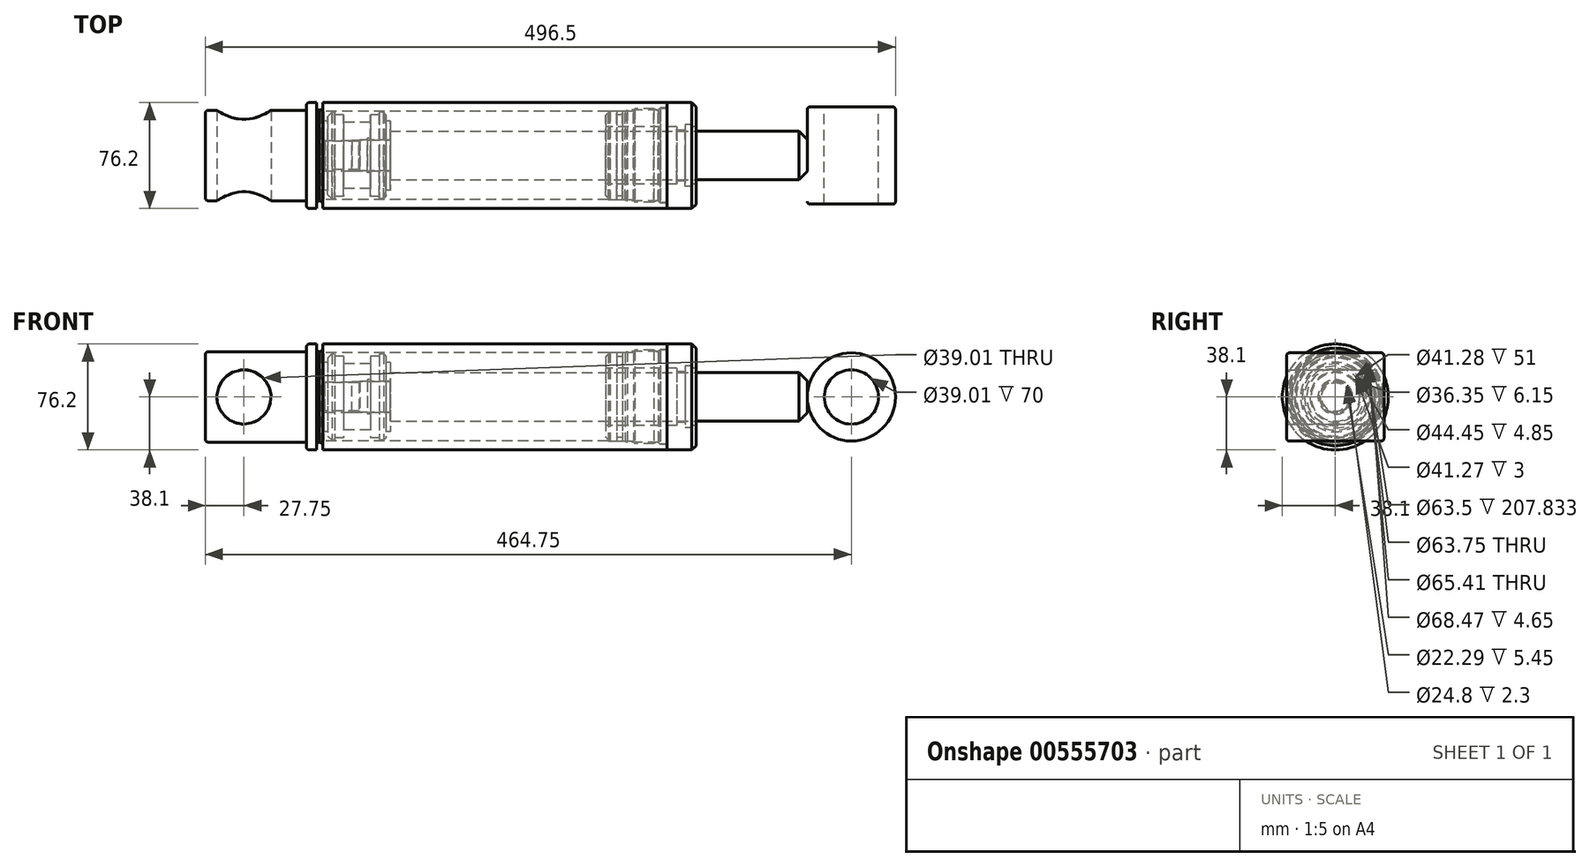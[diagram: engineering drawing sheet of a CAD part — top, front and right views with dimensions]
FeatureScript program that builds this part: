
annotation { "Feature Type Name" : "Feature", "Feature Type Description" : "" }
export const myFeature = defineFeature(function(context is Context, id is Id, definition is map)
    precondition{}
    {
        {
            var Q0;
            Q0=qCreatedBy(makeId("Front.planeOp"),FACE);
            var sketch = newSketch(context, id + "F0", { "sketchPlane" : qUnion([Q0])});
            skLineSegment(sketch, "E0", {"start": v(0, 0) * mm, "end": v(0, 31.22) * mm});
            skArc(sketch, "E1", {"start": v(0, 31.23) * mm, "mid": v(-0.15, 31.58) * mm, "end": v(-0.5, 31.73) * mm});
            skLineSegment(sketch, "E2", {"start": v(-0.5, 31.73) * mm, "end": v(-1.72, 31.73) * mm});
            skLineSegment(sketch, "E3", {"start": v(-1.72, 31.73) * mm, "end": v(-2.42, 31.37) * mm});
            skArc(sketch, "E4", {"start": v(-2.42, 31.37) * mm, "mid": v(-2.8, 31.38) * mm, "end": v(-3, 31.73) * mm});
            skLineSegment(sketch, "E5", {"start": v(-3, 31.73) * mm, "end": v(-3, 32.62) * mm});
            skArc(sketch, "E6", {"start": v(-5, 34.62) * mm, "mid": v(-4.41, 33.21) * mm, "end": v(-3, 32.62) * mm});
            skLineSegment(sketch, "E7", {"start": v(-5, 34.62) * mm, "end": v(-5, 38.1) * mm});
            skLineSegment(sketch, "E8", {"start": v(-5, 38.1) * mm, "end": v(-10.25, 38.1) * mm});
            skArc(sketch, "E9", {"start": v(-10.25, 38.1) * mm, "mid": v(-11.66, 37.51) * mm, "end": v(-12.25, 36.1) * mm});
            skLineSegment(sketch, "E10", {"start": v(-12.25, 36.1) * mm, "end": v(-12.25, 33.3) * mm});
            skLineSegment(sketch, "E11", {"start": v(-13.05, 32.5) * mm, "end": v(-83, 32.5) * mm});
            skArc(sketch, "E12", {"start": v(-83, 32.5) * mm, "mid": v(-84.41, 31.91) * mm, "end": v(-85, 30.5) * mm});
            skLineSegment(sketch, "E13", {"start": v(-85, 30.5) * mm, "end": v(-85, 0) * mm});
            skLineSegment(sketch, "E14", {"start": v(-85, 0) * mm, "end": v(0, 0) * mm});
            skPoint(sketch, "E15.visualSharp", {"position": v(-12.25, 32.5) * mm});
            skArc(sketch, "E15.filletArc", {"start": v(-13.05, 32.5) * mm, "mid": v(-12.48, 32.73) * mm, "end": v(-12.25, 33.3) * mm});
            skSolve(sketch);
        }
        {
            var Q0;
            Q0 = qSketchRegion(id + "F0", true);
            var Q1;
            Q1=sQuery(id+"F0.wireOp",EDGE,"E14");
            revolve(context, id + "F1", {"entities" : qUnion([Q0]), "axis" : qUnion([Q1]), "revolveType" : RevolveType.FULL});
        }
        {
            var Q0;
            Q0=qCreatedBy(makeId("Front.planeOp"),FACE);
            var sketch = newSketch(context, id + "F2", { "sketchPlane" : qUnion([Q0])});
            skCircle(sketch, "E16", {"center": v(-57.25, 0) * mm, "radius": 19.5 * mm});
            skSolve(sketch);
        }
        {
            var Q0;
            Q0=makeQuery(id+"F2.imprint","IMPRINT",FACE,{"disambiguationData":[TD([[makeQuery(id+"F2.imprint","IMPRINT",EDGE,{"derivedFrom":sQuery(id+"F2.wireOp",EDGE,"E16")}),1.0]])]});
            extrude(context, id + "F3", {"entities" : qUnion([Q0]), "operationType" : NewBodyOperationType.REMOVE, "endBound" : BoundingType.THROUGH_ALL, "oppositeDirection" : true, "depth" : 25 * mm, "offsetDistance" : 25 * mm, "hasSecondDirection" : true, "secondDirectionBound" : BoundingType.THROUGH_ALL, "secondDirectionOppositeDirection" : false, "secondDirectionDepth" : 25 * mm});
        }
        {
            var Q0;
            Q0=qCreatedBy(makeId("Front.planeOp"),FACE);
            var sketch = newSketch(context, id + "F4", { "sketchPlane" : qUnion([Q0])});
            skLineSegment(sketch, "E17", {"start": v(0, 25) * mm, "end": v(3, 25) * mm});
            skLineSegment(sketch, "E18", {"start": v(3, 25) * mm, "end": v(3, 28.05) * mm});
            skLineSegment(sketch, "E19", {"start": v(3, 28.05) * mm, "end": v(6, 31.05) * mm});
            skLineSegment(sketch, "E20", {"start": v(6, 31.05) * mm, "end": v(7.9, 31.05) * mm});
            skLineSegment(sketch, "E21", {"start": v(7.9, 31.05) * mm, "end": v(7.9, 29.45) * mm});
            skLineSegment(sketch, "E22", {"start": v(7.9, 29.45) * mm, "end": v(14.25, 29.45) * mm});
            skLineSegment(sketch, "E23", {"start": v(14.25, 29.45) * mm, "end": v(14.25, 23.8) * mm});
            skLineSegment(sketch, "E24", {"start": v(14.25, 23.8) * mm, "end": v(33.75, 23.81) * mm});
            skLineSegment(sketch, "E25", {"start": v(33.75, 23.81) * mm, "end": v(33.75, 12.4) * mm});
            skLineSegment(sketch, "E26", {"start": v(33.75, 12.4) * mm, "end": v(31.45, 12.4) * mm});
            skLineSegment(sketch, "E27", {"start": v(31.45, 12.4) * mm, "end": v(31.45, 11.15) * mm});
            skLineSegment(sketch, "E28", {"start": v(31.45, 11.14) * mm, "end": v(26, 11.14) * mm});
            skLineSegment(sketch, "E29", {"start": v(0, 25) * mm, "end": v(0, 11.14) * mm});
            skLineSegment(sketch, "E30", {"start": v(0, 11.14) * mm, "end": v(0.59, 10.12) * mm});
            skLineSegment(sketch, "E31", {"start": v(0.59, 10.12) * mm, "end": v(25.41, 10.12) * mm});
            skLineSegment(sketch, "E32", {"start": v(25.41, 10.12) * mm, "end": v(26, 11.15) * mm});
            skLineSegment(sketch, "E33", {"start": v(0, 0) * mm, "end": v(54.85, 0) * mm, "construction": true});
            skSolve(sketch);
        }
        {
            var Q0;
            Q0=makeQuery(id+"F4.imprint","IMPRINT",FACE,{"disambiguationData":[TD([[makeQuery(id+"F4.imprint","IMPRINT",EDGE,{"derivedFrom":sQuery(id+"F4.wireOp",EDGE,"E17")}),-1.0]])]});
            var Q1;
            Q1=sQuery(id+"F4.wireOp",EDGE,"E33");
            revolve(context, id + "F5", {"entities" : qUnion([Q0]), "axis" : qUnion([Q1]), "revolveType" : RevolveType.FULL});
        }
        {
            var Q0;
            Q0=qCreatedBy(makeId("Front.planeOp"),FACE);
            var sketch = newSketch(context, id + "F6", { "sketchPlane" : qUnion([Q0])});
            skLineSegment(sketch, "E34", {"start": v(33.75, 11.13) * mm, "end": v(33.75, 29.45) * mm});
            skLineSegment(sketch, "E35", {"start": v(33.75, 29.45) * mm, "end": v(40.1, 29.45) * mm});
            skLineSegment(sketch, "E36", {"start": v(40.1, 29.45) * mm, "end": v(40.1, 31.05) * mm});
            skLineSegment(sketch, "E37", {"start": v(40.1, 31.05) * mm, "end": v(43.4, 31.05) * mm});
            skLineSegment(sketch, "E38", {"start": v(43.4, 31.05) * mm, "end": v(45, 29.45) * mm});
            skLineSegment(sketch, "E39", {"start": v(45, 29.45) * mm, "end": v(45, 25) * mm});
            skLineSegment(sketch, "E40", {"start": v(45, 25) * mm, "end": v(48, 25) * mm});
            skLineSegment(sketch, "E41", {"start": v(48, 25) * mm, "end": v(48, 11.13) * mm});
            skLineSegment(sketch, "E42", {"start": v(48, 11.13) * mm, "end": v(33.75, 11.13) * mm});
            skPoint(sketch, "E43.orphan", {"position": v(33.75, 0) * mm});
            skLineSegment(sketch, "E44", {"start": v(33.75, 0) * mm, "end": v(71.94, 0) * mm, "construction": true});
            skSolve(sketch);
        }
        {
            var Q0;
            Q0=makeQuery(id+"F6.imprint","IMPRINT",FACE,{"disambiguationData":[TD([[makeQuery(id+"F6.imprint","IMPRINT",EDGE,{"derivedFrom":sQuery(id+"F6.wireOp",EDGE,"E34")}),-1.0]])]});
            var Q1;
            Q1=sQuery(id+"F6.wireOp",EDGE,"E44");
            var Q2;
            Q2=sQuery(id+"F6.wireOp",EDGE,"E44");
            revolve(context, id + "F7", {"entities" : qUnion([Q0]), "surfaceEntities" : qUnion([Q1]), "axis" : qUnion([Q2]), "revolveType" : RevolveType.FULL});
        }
        {
            var Q0;
            Q0=qCreatedBy(makeId("Front.planeOp"),FACE);
            var sketch = newSketch(context, id + "F8", { "sketchPlane" : qUnion([Q0])});
            skLineSegment(sketch, "E45", {"start": v(0.5, 0) * mm, "end": v(0.5, 10.13) * mm});
            skLineSegment(sketch, "E46", {"start": v(0.5, 10.13) * mm, "end": v(1, 11) * mm});
            skLineSegment(sketch, "E47", {"start": v(1, 11) * mm, "end": v(20.33, 11) * mm});
            skLineSegment(sketch, "E48", {"start": v(20.33, 11) * mm, "end": v(20.5, 11.1) * mm});
            skLineSegment(sketch, "E49", {"start": v(20.5, 11.1) * mm, "end": v(48, 11.1) * mm});
            skLineSegment(sketch, "E50", {"start": v(348, 11.46) * mm, "end": v(348, 0) * mm});
            skLineSegment(sketch, "E51", {"start": v(348, 0) * mm, "end": v(0.5, 0) * mm});
            skLineSegment(sketch, "E52", {"start": v(48, 11.1) * mm, "end": v(48, 17.46) * mm});
            skLineSegment(sketch, "E53", {"start": v(48, 17.46) * mm, "end": v(342, 17.46) * mm});
            skLineSegment(sketch, "E54", {"start": v(342, 17.46) * mm, "end": v(348, 11.46) * mm});
            skSolve(sketch);
        }
        {
            var Q0;
            Q0=makeQuery(id+"F8.imprint","IMPRINT",FACE,{"disambiguationData":[TD([[makeQuery(id+"F8.imprint","IMPRINT",EDGE,{"derivedFrom":sQuery(id+"F8.wireOp",EDGE,"E45")}),-1.0]])]});
            var Q1;
            Q1=sQuery(id+"F8.wireOp",EDGE,"E51");
            revolve(context, id + "F9", {"entities" : qUnion([Q0]), "axis" : qUnion([Q1]), "revolveType" : RevolveType.FULL});
        }
        {
            var Q0;
            Q0=qCreatedBy(makeId("Front.planeOp"),FACE);
            var sketch = newSketch(context, id + "F10", { "sketchPlane" : qUnion([Q0])});
            skCircle(sketch, "E55", {"center": v(379.75, 0) * mm, "radius": 31.75 * mm});
            skCircle(sketch, "E56", {"center": v(379.75, 0) * mm, "radius": 19.5 * mm});
            skSolve(sketch);
        }
        {
            var Q0;
            Q0=makeQuery(id+"F10.imprint","IMPRINT",FACE,{"disambiguationData":[TD([[makeQuery(id+"F10.imprint","IMPRINT",EDGE,{"derivedFrom":sQuery(id+"F10.wireOp",EDGE,"E55")}),1.0]])]});
            extrude(context, id + "F11", {"entities" : qUnion([Q0]), "depth" : 35 * mm, "offsetDistance" : 25 * mm, "hasSecondDirection" : true, "secondDirectionOppositeDirection" : true, "secondDirectionDepth" : 35 * mm});
        }
        {
            var Q0;
            Q0=makeQuery(id+"F11.opExtrude","CAP_EDGE",EDGE,{"disambiguationData":[OSD([sQuery(id+"F10.wireOp",EDGE,"E55")])],"isStart":true});
            var Q1;
            Q1=makeQuery(id+"F11.opExtrude","CAP_EDGE",EDGE,{"disambiguationData":[OSD([sQuery(id+"F10.wireOp",EDGE,"E55")])],"isStart":false});
            fillet(context, id + "F12", {"entities" : qUnion([Q0, Q1]), "radius" : 2 * mm, "tangentPropagation" : true, "allowEdgeOverflow" : false});
        }
        {
            var Q0;
            Q0=qCreatedBy(makeId("Front.planeOp"),FACE);
            var sketch = newSketch(context, id + "F13", { "sketchPlane" : qUnion([Q0])});
            skLineSegment(sketch, "E57", {"start": v(-3, 31.75) * mm, "end": v(204.83, 31.75) * mm});
            skLineSegment(sketch, "E58", {"start": v(204.83, 31.75) * mm, "end": v(205.05, 31.88) * mm});
            skLineSegment(sketch, "E59", {"start": v(205.05, 31.88) * mm, "end": v(217.01, 31.88) * mm});
            skLineSegment(sketch, "E60", {"start": v(217.01, 31.88) * mm, "end": v(218.45, 32.7) * mm});
            skLineSegment(sketch, "E61", {"start": v(218.45, 32.7) * mm, "end": v(240.82, 32.7) * mm});
            skLineSegment(sketch, "E62", {"start": v(240.82, 32.7) * mm, "end": v(242.35, 34.24) * mm});
            skLineSegment(sketch, "E63", {"start": v(242.35, 34.24) * mm, "end": v(247, 34.24) * mm});
            skLineSegment(sketch, "E64", {"start": v(247, 34.24) * mm, "end": v(247, 38.1) * mm});
            skLineSegment(sketch, "E65", {"start": v(247, 38.1) * mm, "end": v(-0.5, 38.1) * mm});
            skLineSegment(sketch, "E66", {"start": v(-0.5, 38.1) * mm, "end": v(-0.5, 35.12) * mm});
            skArc(sketch, "E67", {"start": v(-0.5, 35.12) * mm, "mid": v(-1.23, 33.36) * mm, "end": v(-3, 32.62) * mm});
            skLineSegment(sketch, "E68", {"start": v(-3, 32.62) * mm, "end": v(-3, 31.75) * mm});
            skLineSegment(sketch, "E69", {"start": v(0, 0) * mm, "end": v(80.8, 0) * mm, "construction": true});
            skSolve(sketch);
        }
        {
            var Q0;
            Q0 = qSketchRegion(id + "F13", true);
            var Q1;
            Q1=sQuery(id+"F13.wireOp",EDGE,"E69");
            revolve(context, id + "F14", {"entities" : qUnion([Q0]), "axis" : qUnion([Q1]), "revolveType" : RevolveType.FULL});
        }
        {
            var Q0;
            Q0=qCreatedBy(makeId("Front.planeOp"),FACE);
            var sketch = newSketch(context, id + "F15", { "sketchPlane" : qUnion([Q0])});
            skLineSegment(sketch, "E70", {"start": v(247, 38.1) * mm, "end": v(265, 38.1) * mm});
            skLineSegment(sketch, "E71", {"start": v(265, 38.1) * mm, "end": v(268, 35.1) * mm});
            skLineSegment(sketch, "E72", {"start": v(268, 35.1) * mm, "end": v(268, 20.64) * mm});
            skLineSegment(sketch, "E73", {"start": v(268, 20.64) * mm, "end": v(265, 20.64) * mm});
            skLineSegment(sketch, "E74", {"start": v(265, 20.64) * mm, "end": v(265, 22.23) * mm});
            skLineSegment(sketch, "E75", {"start": v(265, 22.23) * mm, "end": v(260.15, 22.23) * mm});
            skLineSegment(sketch, "E76", {"start": v(260.15, 22.23) * mm, "end": v(260.15, 18.18) * mm});
            skLineSegment(sketch, "E77", {"start": v(260.15, 18.18) * mm, "end": v(254, 18.18) * mm});
            skLineSegment(sketch, "E78", {"start": v(254, 18.18) * mm, "end": v(254, 20.64) * mm});
            skLineSegment(sketch, "E79", {"start": v(254, 20.64) * mm, "end": v(203, 20.64) * mm});
            skLineSegment(sketch, "E80", {"start": v(203, 20.64) * mm, "end": v(203, 28.91) * mm});
            skLineSegment(sketch, "E81", {"start": v(203, 28.91) * mm, "end": v(206, 31.91) * mm});
            skLineSegment(sketch, "E82", {"start": v(206, 31.91) * mm, "end": v(211, 31.91) * mm});
            skLineSegment(sketch, "E83", {"start": v(211, 31.91) * mm, "end": v(211, 29.15) * mm});
            skLineSegment(sketch, "E84", {"start": v(211, 29.15) * mm, "end": v(215, 29.15) * mm});
            skLineSegment(sketch, "E85", {"start": v(215, 29.15) * mm, "end": v(215, 31.91) * mm});
            skLineSegment(sketch, "E86", {"start": v(215, 31.91) * mm, "end": v(223, 31.91) * mm});
            skLineSegment(sketch, "E87", {"start": v(223, 31.91) * mm, "end": v(224, 33.63) * mm});
            skLineSegment(sketch, "E88", {"start": v(224, 33.63) * mm, "end": v(237.7, 33.63) * mm});
            skLineSegment(sketch, "E89", {"start": v(237.7, 33.63) * mm, "end": v(241, 31.91) * mm});
            skLineSegment(sketch, "E90", {"start": v(241, 31.91) * mm, "end": v(242.5, 31.91) * mm});
            skLineSegment(sketch, "E91", {"start": v(242.5, 31.91) * mm, "end": v(242.5, 33.83) * mm});
            skLineSegment(sketch, "E92", {"start": v(242.5, 33.83) * mm, "end": v(247, 33.83) * mm});
            skLineSegment(sketch, "E93", {"start": v(247, 33.83) * mm, "end": v(247, 38.1) * mm});
            skLineSegment(sketch, "E94", {"start": v(0, 0) * mm, "end": v(276, 0) * mm, "construction": true});
            skSolve(sketch);
        }
        {
            var Q0;
            Q0=makeQuery(id+"F15.imprint","IMPRINT",FACE,{"disambiguationData":[TD([[makeQuery(id+"F15.imprint","IMPRINT",EDGE,{"derivedFrom":sQuery(id+"F15.wireOp",EDGE,"E70")}),-1.0]])]});
            var Q1;
            Q1=sQuery(id+"F15.wireOp",EDGE,"E94");
            revolve(context, id + "F16", {"entities" : qUnion([Q0]), "axis" : qUnion([Q1]), "revolveType" : RevolveType.FULL});
        }
    });
